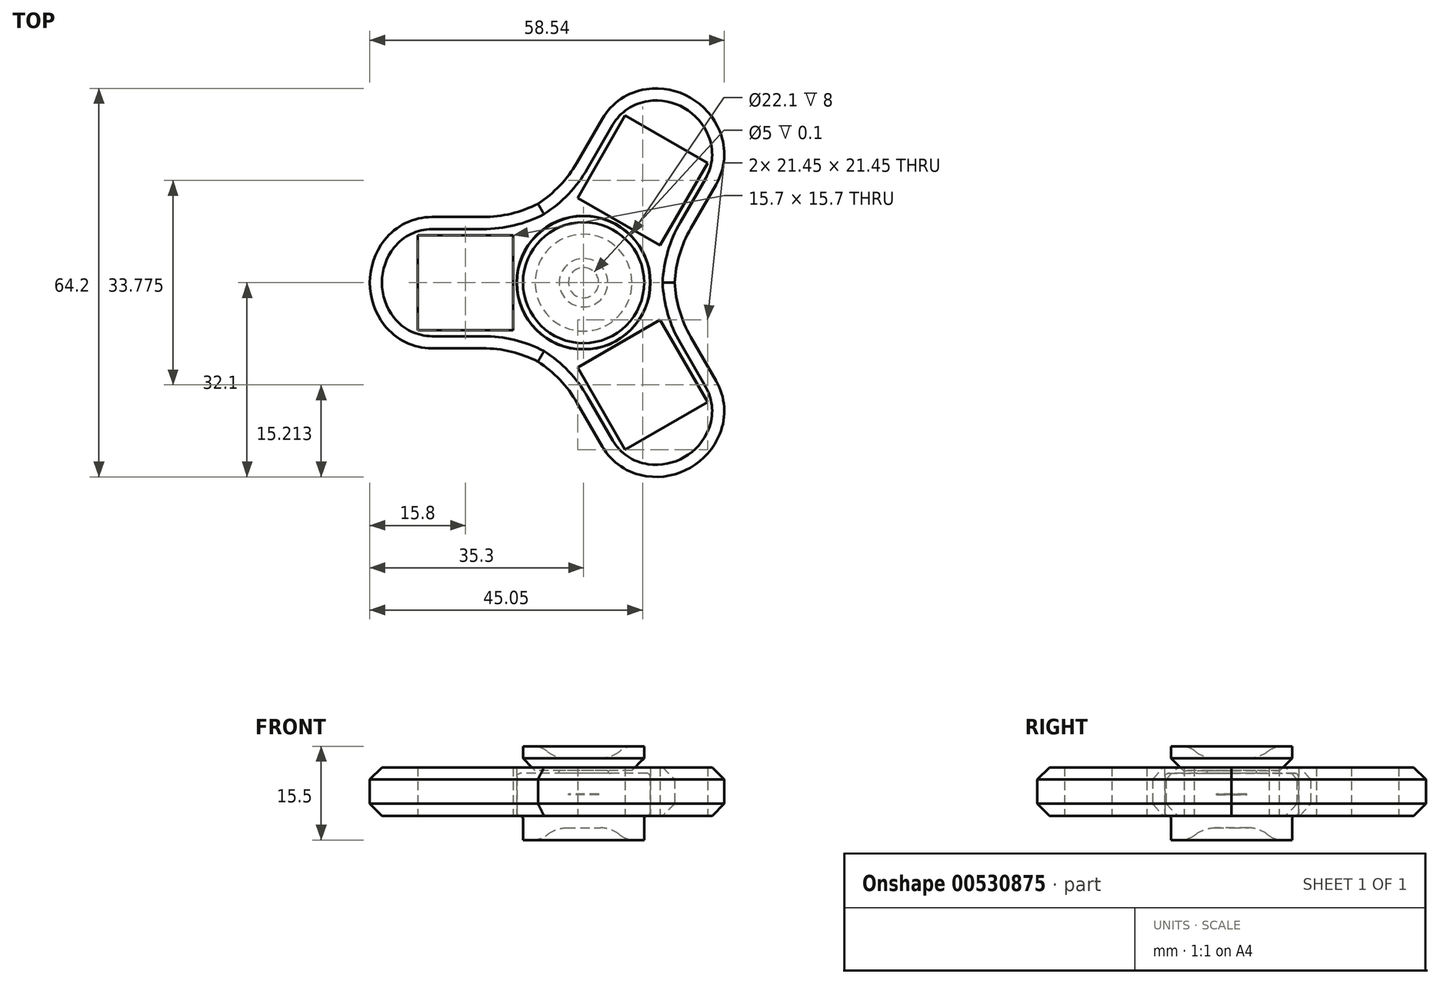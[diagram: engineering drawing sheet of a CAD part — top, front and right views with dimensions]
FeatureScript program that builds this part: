
annotation { "Feature Type Name" : "Feature", "Feature Type Description" : "" }
export const myFeature = defineFeature(function(context is Context, id is Id, definition is map)
    precondition{}
    {
        {
            var Q0;
            Q0=qCreatedBy(makeId("Top.planeOp"),FACE);
            var sketch = newSketch(context, id + "F0", { "sketchPlane" : qUnion([Q0])});
            skCircle(sketch, "E0", {"center": v(0, 0) * mm, "radius": 11 * mm});
            skCircle(sketch, "E1", {"center": v(0, 0) * mm, "radius": 4 * mm});
            skSolve(sketch);
        }
        {
            var Q0;
            Q0=makeQuery(id+"F0.imprint","IMPRINT",FACE,{"disambiguationData":[TD([[makeQuery(id+"F0.imprint","IMPRINT",EDGE,{"derivedFrom":sQuery(id+"F0.wireOp",EDGE,"E0")}),1.0]])]});
            extrude(context, id + "F1", {"entities" : qUnion([Q0]), "depth" : 7 * mm, "offsetDistance" : 25 * mm});
        }
        {
            var Q0;
            Q0=makeQuery(id+"F1.opExtrude","CAP_FACE",FACE,{"disambiguationData":[OSD([sQuery(id+"F0.wireOp",EDGE,"E0"),sQuery(id+"F0.wireOp",EDGE,"E1")])],"isStart":true});
            var sketch = newSketch(context, id + "F2", { "sketchPlane" : qUnion([Q0])});
            skCircle(sketch, "E2.0", {"center": v(0, 0) * mm, "radius": 11.05 * mm});
            skCircle(sketch, "E3.0", {"center": v(0, 0) * mm, "radius": 15.05 * mm});
            skLineSegment(sketch, "E4", {"start": v(0, 0) * mm, "end": v(-19.5, 0) * mm, "construction": true});
            skLineSegment(sketch, "E5.bottom", {"start": v(-27.35, -7.85) * mm, "end": v(-11.65, -7.85) * mm});
            skLineSegment(sketch, "E5.top", {"start": v(-27.35, 7.85) * mm, "end": v(-11.65, 7.85) * mm});
            skLineSegment(sketch, "E5.left", {"start": v(-27.35, -7.85) * mm, "end": v(-27.35, 7.85) * mm});
            skLineSegment(sketch, "E5.right", {"start": v(-11.65, -7.85) * mm, "end": v(-11.65, 7.85) * mm});
            skPoint(sketch, "E5.middle", {"position": v(-19.5, 0) * mm});
            skCircle(sketch, "E6", {"center": v(0, 0) * mm, "radius": 50 * mm, "construction": true});
            skLineSegment(sketch, "E7", {"start": v(-19.5, 0) * mm, "end": v(-35.3, 0) * mm, "construction": true});
            skLineSegment(sketch, "E8", {"start": v(-27.35, 7.85) * mm, "end": v(-27.35, 10.85) * mm, "construction": true});
            skLineSegment(sketch, "E9.0", {"start": v(-23, 10.85) * mm, "end": v(-27.35, 10.85) * mm});
            skLineSegment(sketch, "E9.1", {"start": v(0, 10.85) * mm, "end": v(-2.1, 10.85) * mm, "construction": true});
            skLineSegment(sketch, "E10.trimOffspring", {"start": v(-10.43, 10.85) * mm, "end": v(-23, 10.85) * mm});
            skLineSegment(sketch, "E11.MirrorCS", {"start": v(-10.43, -10.85) * mm, "end": v(-23, -10.85) * mm});
            skLineSegment(sketch, "E12.MirrorCS", {"start": v(-23, -10.85) * mm, "end": v(-27.35, -10.85) * mm});
            skArc(sketch, "E13", {"start": v(-27.35, 10.85) * mm, "mid": v(-35.3, 0) * mm, "end": v(-27.35, -10.85) * mm});
            skLineSegment(sketch, "E14.1.0", {"start": v(20.47, -19.76) * mm, "end": v(12.62, -6.16) * mm});
            skLineSegment(sketch, "E14.1.1", {"start": v(12.62, -6.16) * mm, "end": v(-0.97, -14.01) * mm});
            skLineSegment(sketch, "E14.1.2", {"start": v(6.88, -27.61) * mm, "end": v(-0.97, -14.01) * mm});
            skLineSegment(sketch, "E14.1.3", {"start": v(-4.18, -14.46) * mm, "end": v(2.1, -25.34) * mm});
            skLineSegment(sketch, "E14.1.4", {"start": v(2.1, -25.34) * mm, "end": v(4.28, -29.11) * mm});
            skLineSegment(sketch, "E14.1.5", {"start": v(20.47, -19.76) * mm, "end": v(6.88, -27.61) * mm});
            skArc(sketch, "E14.1.6", {"start": v(4.28, -29.11) * mm, "mid": v(17.65, -30.57) * mm, "end": v(23.07, -18.26) * mm});
            skLineSegment(sketch, "E14.1.7", {"start": v(20.9, -14.5) * mm, "end": v(23.07, -18.26) * mm});
            skLineSegment(sketch, "E14.1.8", {"start": v(14.61, -3.6) * mm, "end": v(20.9, -14.5) * mm});
            skLineSegment(sketch, "E14.2.0", {"start": v(6.88, 27.61) * mm, "end": v(-0.97, 14.01) * mm});
            skLineSegment(sketch, "E14.2.1", {"start": v(-0.97, 14.01) * mm, "end": v(12.62, 6.16) * mm});
            skLineSegment(sketch, "E14.2.2", {"start": v(20.47, 19.76) * mm, "end": v(12.62, 6.16) * mm});
            skLineSegment(sketch, "E14.2.3", {"start": v(14.61, 3.6) * mm, "end": v(20.9, 14.5) * mm});
            skLineSegment(sketch, "E14.2.4", {"start": v(20.9, 14.5) * mm, "end": v(23.07, 18.26) * mm});
            skLineSegment(sketch, "E14.2.5", {"start": v(6.88, 27.61) * mm, "end": v(20.47, 19.76) * mm});
            skArc(sketch, "E14.2.6", {"start": v(23.07, 18.26) * mm, "mid": v(17.65, 30.57) * mm, "end": v(4.28, 29.11) * mm});
            skLineSegment(sketch, "E14.2.7", {"start": v(2.1, 25.34) * mm, "end": v(4.28, 29.11) * mm});
            skLineSegment(sketch, "E14.2.8", {"start": v(-4.18, 14.46) * mm, "end": v(2.1, 25.34) * mm});
            skCircle(sketch, "E15", {"center": v(0, 0) * mm, "radius": 29.42 * mm, "construction": true});
            skSolve(sketch);
        }
        {
            var Q0;
            {var subQ5=sQuery(id+"F2.wireOp",EDGE,"E14.2.0");Q0=makeQuery(id+"F2.imprint","IMPRINT",FACE,{"disambiguationData":[TD([[makeQuery(id+"F2.imprint","IMPRINT",EDGE,{"derivedFrom":subQ5}),-1.0]])]});}
            var Q1;
            Q1=makeQuery(id+"F2.imprint","IMPRINT",FACE,{"disambiguationData":[TD([[makeQuery(id+"F2.imprint","IMPRINT",EDGE,{"derivedFrom":sQuery(id+"F2.wireOp",EDGE,"E2.0")}),-1.0]])]});
            var Q2;
            {var subQ6=sQuery(id+"F2.wireOp",EDGE,"E14.1.0");Q2=makeQuery(id+"F2.imprint","IMPRINT",FACE,{"disambiguationData":[TD([[makeQuery(id+"F2.imprint","IMPRINT",EDGE,{"derivedFrom":subQ6}),-1.0]])]});}
            var Q3;
            {var subQ5=sQuery(id+"F2.wireOp",EDGE,"E5.bottom");Q3=makeQuery(id+"F2.imprint","IMPRINT",FACE,{"disambiguationData":[TD([[makeQuery(id+"F2.imprint","IMPRINT",EDGE,{"derivedFrom":subQ5}),-1.0]])]});}
            extrude(context, id + "F3", {"entities" : qUnion([Q0, Q1, Q2, Q3]), "oppositeDirection" : true, "depth" : 8 * mm, "offsetDistance" : 25 * mm});
        }
        {
            var Q0;
            Q0=makeQuery(id+"F3.opExtrude","SWEPT_EDGE",EDGE,{"disambiguationData":[OSD([sQuery(id+"F2.wireOp",EDGE,"E3.0"),sQuery(id+"F2.wireOp",EDGE,"E14.2.3")])]});
            var Q1;
            Q1=makeQuery(id+"F3.opExtrude","SWEPT_EDGE",EDGE,{"disambiguationData":[OSD([sQuery(id+"F2.wireOp",EDGE,"E3.0"),sQuery(id+"F2.wireOp",EDGE,"E14.1.8")])]});
            var Q2;
            Q2=makeQuery(id+"F3.opExtrude","SWEPT_EDGE",EDGE,{"disambiguationData":[OSD([sQuery(id+"F2.wireOp",EDGE,"E3.0"),sQuery(id+"F2.wireOp",EDGE,"E14.2.8")])]});
            var Q3;
            Q3=makeQuery(id+"F3.opExtrude","SWEPT_EDGE",EDGE,{"disambiguationData":[OSD([sQuery(id+"F2.wireOp",EDGE,"E3.0"),sQuery(id+"F2.wireOp",EDGE,"E10.trimOffspring")])]});
            var Q4;
            Q4=makeQuery(id+"F3.opExtrude","SWEPT_EDGE",EDGE,{"disambiguationData":[OSD([sQuery(id+"F2.wireOp",EDGE,"E3.0"),sQuery(id+"F2.wireOp",EDGE,"E11.MirrorCS")])]});
            var Q5;
            Q5=makeQuery(id+"F3.opExtrude","SWEPT_EDGE",EDGE,{"disambiguationData":[OSD([sQuery(id+"F2.wireOp",EDGE,"E3.0"),sQuery(id+"F2.wireOp",EDGE,"E14.1.3")])]});
            fillet(context, id + "F4", {"entities" : qUnion([Q0, Q1, Q2, Q3, Q4, Q5]), "radius" : 20 * mm, "tangentPropagation" : true, "allowEdgeOverflow" : false});
        }
        {
            var Q0;
            Q0=makeQuery(id+"F3.opExtrude","SWEPT_EDGE",EDGE,{"disambiguationData":[OSD([sQuery(id+"F2.wireOp",EDGE,"E14.2.4"),sQuery(id+"F2.wireOp",EDGE,"E14.2.6")])]});
            var Q1;
            Q1=makeQuery(id+"F3.opExtrude","SWEPT_EDGE",EDGE,{"disambiguationData":[OSD([sQuery(id+"F2.wireOp",EDGE,"E14.2.6"),sQuery(id+"F2.wireOp",EDGE,"E14.2.7")])]});
            var Q2;
            Q2=makeQuery(id+"F3.opExtrude","SWEPT_EDGE",EDGE,{"disambiguationData":[OSD([sQuery(id+"F2.wireOp",EDGE,"E9.0"),sQuery(id+"F2.wireOp",EDGE,"E13")])]});
            var Q3;
            Q3=makeQuery(id+"F3.opExtrude","SWEPT_EDGE",EDGE,{"disambiguationData":[OSD([sQuery(id+"F2.wireOp",EDGE,"E12.MirrorCS"),sQuery(id+"F2.wireOp",EDGE,"E13")])]});
            var Q4;
            Q4=makeQuery(id+"F3.opExtrude","SWEPT_EDGE",EDGE,{"disambiguationData":[OSD([sQuery(id+"F2.wireOp",EDGE,"E14.1.4"),sQuery(id+"F2.wireOp",EDGE,"E14.1.6")])]});
            var Q5;
            Q5=makeQuery(id+"F3.opExtrude","SWEPT_EDGE",EDGE,{"disambiguationData":[OSD([sQuery(id+"F2.wireOp",EDGE,"E14.1.6"),sQuery(id+"F2.wireOp",EDGE,"E14.1.7")])]});
            fillet(context, id + "F5", {"entities" : qUnion([Q0, Q1, Q2, Q3, Q4, Q5]), "radius" : 10 * mm, "tangentPropagation" : true, "allowEdgeOverflow" : false});
        }
        {
            var Q0;
            Q0=makeQuery(id+"F3.opExtrude","CAP_EDGE",EDGE,{"disambiguationData":[OSD([sQuery(id+"F2.wireOp",EDGE,"E14.2.6")])],"isStart":false});
            var Q1;
            Q1=makeQuery(id+"F3.opExtrude","CAP_EDGE",EDGE,{"disambiguationData":[OSD([sQuery(id+"F2.wireOp",EDGE,"E14.1.6")])],"isStart":false});
            var Q2;
            {var subQ0=sQuery(id+"F2.wireOp",EDGE,"E13");var subQ1=sQuery(id+"F2.wireOp",EDGE,"E9.0");Q2=makeQuery(id+"F5.opFillet","BLEND_EDGE",EDGE,{"blendedFrom":[makeQuery(id+"F3.opExtrude","SWEPT_EDGE",EDGE,{"disambiguationData":[OSD([subQ1,subQ0])]}),makeQuery(id+"F3.opExtrude","CAP_FACE",FACE,{"disambiguationData":[OSD([sQuery(id+"F2.wireOp",EDGE,"E2.0"),sQuery(id+"F2.wireOp",EDGE,"E3.0"),sQuery(id+"F2.wireOp",EDGE,"E5.bottom"),sQuery(id+"F2.wireOp",EDGE,"E5.top"),sQuery(id+"F2.wireOp",EDGE,"E5.left"),sQuery(id+"F2.wireOp",EDGE,"E5.right"),subQ1,sQuery(id+"F2.wireOp",EDGE,"E10.trimOffspring"),sQuery(id+"F2.wireOp",EDGE,"E11.MirrorCS"),sQuery(id+"F2.wireOp",EDGE,"E12.MirrorCS"),subQ0,sQuery(id+"F2.wireOp",EDGE,"E14.1.0"),sQuery(id+"F2.wireOp",EDGE,"E14.1.1"),sQuery(id+"F2.wireOp",EDGE,"E14.1.2"),sQuery(id+"F2.wireOp",EDGE,"E14.1.3"),sQuery(id+"F2.wireOp",EDGE,"E14.1.4"),sQuery(id+"F2.wireOp",EDGE,"E14.1.5"),sQuery(id+"F2.wireOp",EDGE,"E14.1.6"),sQuery(id+"F2.wireOp",EDGE,"E14.1.7"),sQuery(id+"F2.wireOp",EDGE,"E14.1.8"),sQuery(id+"F2.wireOp",EDGE,"E14.2.0"),sQuery(id+"F2.wireOp",EDGE,"E14.2.1"),sQuery(id+"F2.wireOp",EDGE,"E14.2.2"),sQuery(id+"F2.wireOp",EDGE,"E14.2.3"),sQuery(id+"F2.wireOp",EDGE,"E14.2.4"),sQuery(id+"F2.wireOp",EDGE,"E14.2.5"),sQuery(id+"F2.wireOp",EDGE,"E14.2.6"),sQuery(id+"F2.wireOp",EDGE,"E14.2.7"),sQuery(id+"F2.wireOp",EDGE,"E14.2.8")])],"isStart":false})],"blendedInto":[makeQuery(id+"F3.opExtrude","CAP_FACE",FACE,{"disambiguationData":[OSD([sQuery(id+"F2.wireOp",EDGE,"E2.0"),sQuery(id+"F2.wireOp",EDGE,"E3.0"),sQuery(id+"F2.wireOp",EDGE,"E5.bottom"),sQuery(id+"F2.wireOp",EDGE,"E5.top"),sQuery(id+"F2.wireOp",EDGE,"E5.left"),sQuery(id+"F2.wireOp",EDGE,"E5.right"),subQ1,sQuery(id+"F2.wireOp",EDGE,"E10.trimOffspring"),sQuery(id+"F2.wireOp",EDGE,"E11.MirrorCS"),sQuery(id+"F2.wireOp",EDGE,"E12.MirrorCS"),subQ0,sQuery(id+"F2.wireOp",EDGE,"E14.1.0"),sQuery(id+"F2.wireOp",EDGE,"E14.1.1"),sQuery(id+"F2.wireOp",EDGE,"E14.1.2"),sQuery(id+"F2.wireOp",EDGE,"E14.1.3"),sQuery(id+"F2.wireOp",EDGE,"E14.1.4"),sQuery(id+"F2.wireOp",EDGE,"E14.1.5"),sQuery(id+"F2.wireOp",EDGE,"E14.1.6"),sQuery(id+"F2.wireOp",EDGE,"E14.1.7"),sQuery(id+"F2.wireOp",EDGE,"E14.1.8"),sQuery(id+"F2.wireOp",EDGE,"E14.2.0"),sQuery(id+"F2.wireOp",EDGE,"E14.2.1"),sQuery(id+"F2.wireOp",EDGE,"E14.2.2"),sQuery(id+"F2.wireOp",EDGE,"E14.2.3"),sQuery(id+"F2.wireOp",EDGE,"E14.2.4"),sQuery(id+"F2.wireOp",EDGE,"E14.2.5"),sQuery(id+"F2.wireOp",EDGE,"E14.2.6"),sQuery(id+"F2.wireOp",EDGE,"E14.2.7"),sQuery(id+"F2.wireOp",EDGE,"E14.2.8")])],"isStart":false})]});}
            var Q3;
            Q3=makeQuery(id+"F3.opExtrude","CAP_EDGE",EDGE,{"disambiguationData":[OSD([sQuery(id+"F2.wireOp",EDGE,"E14.2.6")])],"isStart":true});
            var Q4;
            Q4=makeQuery(id+"F3.opExtrude","CAP_EDGE",EDGE,{"disambiguationData":[OSD([sQuery(id+"F2.wireOp",EDGE,"E13")])],"isStart":true});
            var Q5;
            Q5=makeQuery(id+"F3.opExtrude","CAP_EDGE",EDGE,{"disambiguationData":[OSD([sQuery(id+"F2.wireOp",EDGE,"E14.1.6")])],"isStart":true});
            chamfer(context, id + "F6", {"entities" : qUnion([Q0, Q1, Q2, Q3, Q4, Q5]), "width" : 2 * mm, "tangentPropagation" : true});
        }
        {
            var Q0;
            Q0=makeQuery(id+"F3.opExtrude","CAP_FACE",FACE,{"disambiguationData":[OSD([sQuery(id+"F2.wireOp",EDGE,"E2.0"),sQuery(id+"F2.wireOp",EDGE,"E3.0"),sQuery(id+"F2.wireOp",EDGE,"E5.bottom"),sQuery(id+"F2.wireOp",EDGE,"E5.top"),sQuery(id+"F2.wireOp",EDGE,"E5.left"),sQuery(id+"F2.wireOp",EDGE,"E5.right"),sQuery(id+"F2.wireOp",EDGE,"E9.0"),sQuery(id+"F2.wireOp",EDGE,"E10.trimOffspring"),sQuery(id+"F2.wireOp",EDGE,"E11.MirrorCS"),sQuery(id+"F2.wireOp",EDGE,"E12.MirrorCS"),sQuery(id+"F2.wireOp",EDGE,"E13"),sQuery(id+"F2.wireOp",EDGE,"E14.1.0"),sQuery(id+"F2.wireOp",EDGE,"E14.1.1"),sQuery(id+"F2.wireOp",EDGE,"E14.1.2"),sQuery(id+"F2.wireOp",EDGE,"E14.1.3"),sQuery(id+"F2.wireOp",EDGE,"E14.1.4"),sQuery(id+"F2.wireOp",EDGE,"E14.1.5"),sQuery(id+"F2.wireOp",EDGE,"E14.1.6"),sQuery(id+"F2.wireOp",EDGE,"E14.1.7"),sQuery(id+"F2.wireOp",EDGE,"E14.1.8"),sQuery(id+"F2.wireOp",EDGE,"E14.2.0"),sQuery(id+"F2.wireOp",EDGE,"E14.2.1"),sQuery(id+"F2.wireOp",EDGE,"E14.2.2"),sQuery(id+"F2.wireOp",EDGE,"E14.2.3"),sQuery(id+"F2.wireOp",EDGE,"E14.2.4"),sQuery(id+"F2.wireOp",EDGE,"E14.2.5"),sQuery(id+"F2.wireOp",EDGE,"E14.2.6"),sQuery(id+"F2.wireOp",EDGE,"E14.2.7"),sQuery(id+"F2.wireOp",EDGE,"E14.2.8")])],"isStart":true});
            var sketch = newSketch(context, id + "F7", { "sketchPlane" : qUnion([Q0])});
            skLineSegment(sketch, "E16.0", {"start": v(21.23, -21.63) * mm, "end": v(8.12, -29.2) * mm});
            skArc(sketch, "E17.0", {"start": v(20.66, -24.22) * mm, "mid": v(21.05, -22.95) * mm, "end": v(21.23, -21.63) * mm});
            skArc(sketch, "E17.1", {"start": v(10.65, -30) * mm, "mid": v(16.65, -28.84) * mm, "end": v(20.66, -24.22) * mm});
            skArc(sketch, "E17.2", {"start": v(8.12, -29.2) * mm, "mid": v(9.35, -29.7) * mm, "end": v(10.65, -30) * mm});
            skArc(sketch, "E18.0", {"start": v(10.65, 30) * mm, "mid": v(9.35, 29.7) * mm, "end": v(8.12, 29.2) * mm});
            skArc(sketch, "E18.1", {"start": v(20.66, 24.22) * mm, "mid": v(16.65, 28.84) * mm, "end": v(10.65, 30) * mm});
            skArc(sketch, "E18.2", {"start": v(21.23, 21.63) * mm, "mid": v(21.05, 22.95) * mm, "end": v(20.66, 24.22) * mm});
            skLineSegment(sketch, "E19.0", {"start": v(8.12, 29.2) * mm, "end": v(21.23, 21.63) * mm});
            skArc(sketch, "E20.0", {"start": v(-31.3, -5.78) * mm, "mid": v(-30.4, -6.76) * mm, "end": v(-29.35, -7.57) * mm});
            skArc(sketch, "E20.1", {"start": v(-31.3, 5.78) * mm, "mid": v(-33.3, 0) * mm, "end": v(-31.3, -5.78) * mm});
            skArc(sketch, "E20.2", {"start": v(-29.35, 7.57) * mm, "mid": v(-30.4, 6.76) * mm, "end": v(-31.3, 5.78) * mm});
            skLineSegment(sketch, "E21.0", {"start": v(-29.35, -7.57) * mm, "end": v(-29.35, 7.57) * mm});
            skSolve(sketch);
        }
        {
            var Q0;
            Q0=makeQuery(id+"F1.opExtrude","CAP_FACE",FACE,{"disambiguationData":[OSD([sQuery(id+"F0.wireOp",EDGE,"E0"),sQuery(id+"F0.wireOp",EDGE,"E1")])],"isStart":true});
            var sketch = newSketch(context, id + "F8", { "sketchPlane" : qUnion([Q0])});
            skCircle(sketch, "E22.0", {"center": v(0, 0) * mm, "radius": 10 * mm});
            skCircle(sketch, "E23.0", {"center": v(0, 0) * mm, "radius": 5 * mm});
            skSolve(sketch);
        }
        {
            var Q0;
            Q0=makeQuery(id+"F8.imprint","IMPRINT",FACE,{"disambiguationData":[TD([[makeQuery(id+"F8.imprint","IMPRINT",EDGE,{"derivedFrom":sQuery(id+"F8.wireOp",EDGE,"E22.0")}),1.0]])]});
            var Q1;
            Q1=makeQuery(id+"F8.imprint","IMPRINT",FACE,{"disambiguationData":[TD([[makeQuery(id+"F8.imprint","IMPRINT",EDGE,{"derivedFrom":sQuery(id+"F8.wireOp",EDGE,"c407c948-2510-426a-b12c-06ac0bc9cf64.0")}),-1.0]])]});
            var Q2;
            Q2=makeQuery(id+"F8.imprint","IMPRINT",FACE,{"disambiguationData":[TD([[makeQuery(id+"F8.imprint","IMPRINT",EDGE,{"derivedFrom":sQuery(id+"F8.wireOp",EDGE,"c407c948-2510-426a-b12c-06ac0bc9cf64.0")}),1.0]])]});
            var Q3;
            Q3=makeQuery(id+"F8.imprint","IMPRINT",FACE,{"disambiguationData":[TD([[makeQuery(id+"F8.imprint","IMPRINT",EDGE,{"derivedFrom":makeQuery(id+"F1.opExtrude","CAP_EDGE",EDGE,{"disambiguationData":[OSD([sQuery(id+"F0.wireOp",EDGE,"E1")])],"isStart":true})}),-1.0]])]});
            var Q4;
            Q4=makeQuery(id+"F8.imprint","IMPRINT",FACE,{"disambiguationData":[TD([[makeQuery(id+"F8.imprint","IMPRINT",EDGE,{"derivedFrom":sQuery(id+"F8.wireOp",EDGE,"E23.0")}),1.0]])]});
            extrude(context, id + "F9", {"entities" : qUnion([Q0, Q1, Q2, Q3, Q4]), "depth" : 2 * mm, "offsetDistance" : 25 * mm});
        }
        {
            var Q0;
            Q0=makeQuery(id+"F8.imprint","IMPRINT",FACE,{"disambiguationData":[TD([[makeQuery(id+"F8.imprint","IMPRINT",EDGE,{"derivedFrom":makeQuery(id+"F1.opExtrude","CAP_EDGE",EDGE,{"disambiguationData":[OSD([sQuery(id+"F0.wireOp",EDGE,"E1")])],"isStart":true})}),-1.0]])]});
            extrude(context, id + "F10", {"entities" : qUnion([Q0]), "operationType" : NewBodyOperationType.ADD, "oppositeDirection" : true, "depth" : 7.5 * mm, "offsetDistance" : 25 * mm});
        }
        {
            var Q0;
            Q0=makeQuery(id+"F8.imprint","IMPRINT",FACE,{"disambiguationData":[TD([[makeQuery(id+"F8.imprint","IMPRINT",EDGE,{"derivedFrom":sQuery(id+"F8.wireOp",EDGE,"E22.0")}),1.0]])]});
            extrude(context, id + "F11", {"entities" : qUnion([Q0]), "operationType" : NewBodyOperationType.ADD, "depth" : 4 * mm, "offsetDistance" : 25 * mm});
        }
        {
            var Q0;
            Q0=makeQuery(id+"F10.opExtrude","CAP_FACE",FACE,{"disambiguationData":[OSD([sQuery(id+"F0.wireOp",EDGE,"E1")])],"isStart":false});
            var sketch = newSketch(context, id + "F12", { "sketchPlane" : qUnion([Q0])});
            skCircle(sketch, "E24.0", {"center": v(0, 0) * mm, "radius": 10 * mm});
            skCircle(sketch, "E25.0", {"center": v(0, 0) * mm, "radius": 2.5 * mm});
            skCircle(sketch, "E26.0", {"center": v(0, 0) * mm, "radius": 5 * mm});
            skSolve(sketch);
        }
        {
            var Q0;
            Q0=makeQuery(id+"F12.imprint","IMPRINT",FACE,{"disambiguationData":[TD([[makeQuery(id+"F12.imprint","IMPRINT",EDGE,{"derivedFrom":sQuery(id+"F12.wireOp",EDGE,"E25.0")}),1.0]])]});
            extrude(context, id + "F13", {"entities" : qUnion([Q0]), "operationType" : NewBodyOperationType.REMOVE, "oppositeDirection" : true, "depth" : 4 * mm, "offsetDistance" : 25 * mm});
        }
        {
            var Q0;
            Q0=makeQuery(id+"F12.imprint","IMPRINT",FACE,{"disambiguationData":[TD([[makeQuery(id+"F12.imprint","IMPRINT",EDGE,{"derivedFrom":sQuery(id+"F12.wireOp",EDGE,"E24.0")}),1.0]])]});
            var Q1;
            Q1=makeQuery(id+"F12.imprint","IMPRINT",FACE,{"disambiguationData":[TD([[makeQuery(id+"F12.imprint","IMPRINT",EDGE,{"derivedFrom":sQuery(id+"F12.wireOp",EDGE,"a1f51509-8c7b-4646-a507-0ed3af852b90.0")}),-1.0]])]});
            var Q2;
            Q2=makeQuery(id+"F12.imprint","IMPRINT",FACE,{"disambiguationData":[TD([[makeQuery(id+"F12.imprint","IMPRINT",EDGE,{"derivedFrom":sQuery(id+"F12.wireOp",EDGE,"15deca98-b56f-4649-b585-fda4b9412a6e.0")}),1.0]])]});
            var Q3;
            Q3=makeQuery(id+"F12.imprint","IMPRINT",FACE,{"disambiguationData":[TD([[makeQuery(id+"F12.imprint","IMPRINT",EDGE,{"derivedFrom":sQuery(id+"F12.wireOp",EDGE,"a1f51509-8c7b-4646-a507-0ed3af852b90.0")}),1.0]])]});
            var Q4;
            Q4=makeQuery(id+"F12.imprint","IMPRINT",FACE,{"disambiguationData":[TD([[makeQuery(id+"F12.imprint","IMPRINT",EDGE,{"derivedFrom":sQuery(id+"F12.wireOp",EDGE,"E25.0")}),-1.0]])]});
            var Q5;
            Q5=makeQuery(id+"F12.imprint","IMPRINT",FACE,{"disambiguationData":[TD([[makeQuery(id+"F12.imprint","IMPRINT",EDGE,{"derivedFrom":sQuery(id+"F12.wireOp",EDGE,"E25.0")}),1.0]])]});
            var Q6;
            Q6=makeQuery(id+"F12.imprint","IMPRINT",FACE,{"disambiguationData":[TD([[makeQuery(id+"F12.imprint","IMPRINT",EDGE,{"derivedFrom":sQuery(id+"F12.wireOp",EDGE,"E26.0")}),1.0]])]});
            extrude(context, id + "F14", {"entities" : qUnion([Q0, Q1, Q2, Q3, Q4, Q5, Q6]), "depth" : 2 * mm, "offsetDistance" : 25 * mm});
        }
        {
            var Q0;
            Q0=makeQuery(id+"F12.imprint","IMPRINT",FACE,{"disambiguationData":[TD([[makeQuery(id+"F12.imprint","IMPRINT",EDGE,{"derivedFrom":sQuery(id+"F12.wireOp",EDGE,"E25.0")}),1.0]])]});
            extrude(context, id + "F15", {"entities" : qUnion([Q0]), "operationType" : NewBodyOperationType.ADD, "oppositeDirection" : true, "depth" : 3.9 * mm, "offsetDistance" : 25 * mm});
        }
        {
            var Q0;
            Q0=makeQuery(id+"F12.imprint","IMPRINT",FACE,{"disambiguationData":[TD([[makeQuery(id+"F12.imprint","IMPRINT",EDGE,{"derivedFrom":sQuery(id+"F12.wireOp",EDGE,"E24.0")}),1.0]])]});
            extrude(context, id + "F16", {"entities" : qUnion([Q0]), "operationType" : NewBodyOperationType.ADD, "depth" : 4 * mm, "offsetDistance" : 25 * mm});
        }
        {
            var Q0;
            Q0=makeQuery(id+"F9.opExtrude","CAP_EDGE",EDGE,{"disambiguationData":[OSD([sQuery(id+"F8.wireOp",EDGE,"E22.0")])],"isStart":true});
            var Q1;
            Q1=makeQuery(id+"F14.opExtrude","CAP_EDGE",EDGE,{"disambiguationData":[OSD([sQuery(id+"F12.wireOp",EDGE,"E24.0")])],"isStart":true});
            chamfer(context, id + "F17", {"entities" : qUnion([Q0, Q1]), "width" : 2 * mm, "tangentPropagation" : true});
        }
        {
            var Q0;
            Q0=makeQuery(id+"F1.opExtrude","CAP_FACE",FACE,{"disambiguationData":[OSD([sQuery(id+"F0.wireOp",EDGE,"E0"),sQuery(id+"F0.wireOp",EDGE,"E1")])],"isStart":true});
            var Q1;
            Q1=makeQuery(id+"F1.opExtrude","CAP_FACE",FACE,{"disambiguationData":[OSD([sQuery(id+"F0.wireOp",EDGE,"E0"),sQuery(id+"F0.wireOp",EDGE,"E1")])],"isStart":false});
            fillet(context, id + "F18", {"entities" : qUnion([Q0, Q1]), "radius" : .5 * mm, "tangentPropagation" : true, "allowEdgeOverflow" : false});
        }
        {
            var Q0;
            Q0=makeQuery(id+"F11.opExtrude","CAP_EDGE",EDGE,{"disambiguationData":[OSD([sQuery(id+"F8.wireOp",EDGE,"E23.0")])],"isStart":false});
            var Q1;
            Q1=makeQuery(id+"F16.opExtrude","CAP_EDGE",EDGE,{"disambiguationData":[OSD([sQuery(id+"F12.wireOp",EDGE,"E26.0")])],"isStart":false});
            fillet(context, id + "F19", {"entities" : qUnion([Q0, Q1]), "radius" : 4 * mm, "tangentPropagation" : true, "allowEdgeOverflow" : false});
        }
        {
            var Q0;
            Q0=makeQuery(id+"F9.opExtrude","CAP_FACE",FACE,{"disambiguationData":[OSD([sQuery(id+"F8.wireOp",EDGE,"E22.0")])],"isStart":false});
            var Q1;
            Q1=makeQuery(id+"F19.opFillet","BLEND_EDGE",EDGE,{"blendedFrom":[makeQuery(id+"F16.opExtrude","CAP_EDGE",EDGE,{"disambiguationData":[OSD([sQuery(id+"F12.wireOp",EDGE,"E26.0")])],"isStart":false}),makeQuery(id+"F14.opExtrude","CAP_FACE",FACE,{"disambiguationData":[OSD([sQuery(id+"F12.wireOp",EDGE,"E24.0")])],"isStart":false})],"blendedInto":[makeQuery(id+"F14.opExtrude","CAP_FACE",FACE,{"disambiguationData":[OSD([sQuery(id+"F12.wireOp",EDGE,"E24.0")])],"isStart":false})]});
            fillet(context, id + "F20", {"entities" : qUnion([Q0, Q1]), "radius" : 5 * mm, "tangentPropagation" : true, "allowEdgeOverflow" : false});
        }
    });
